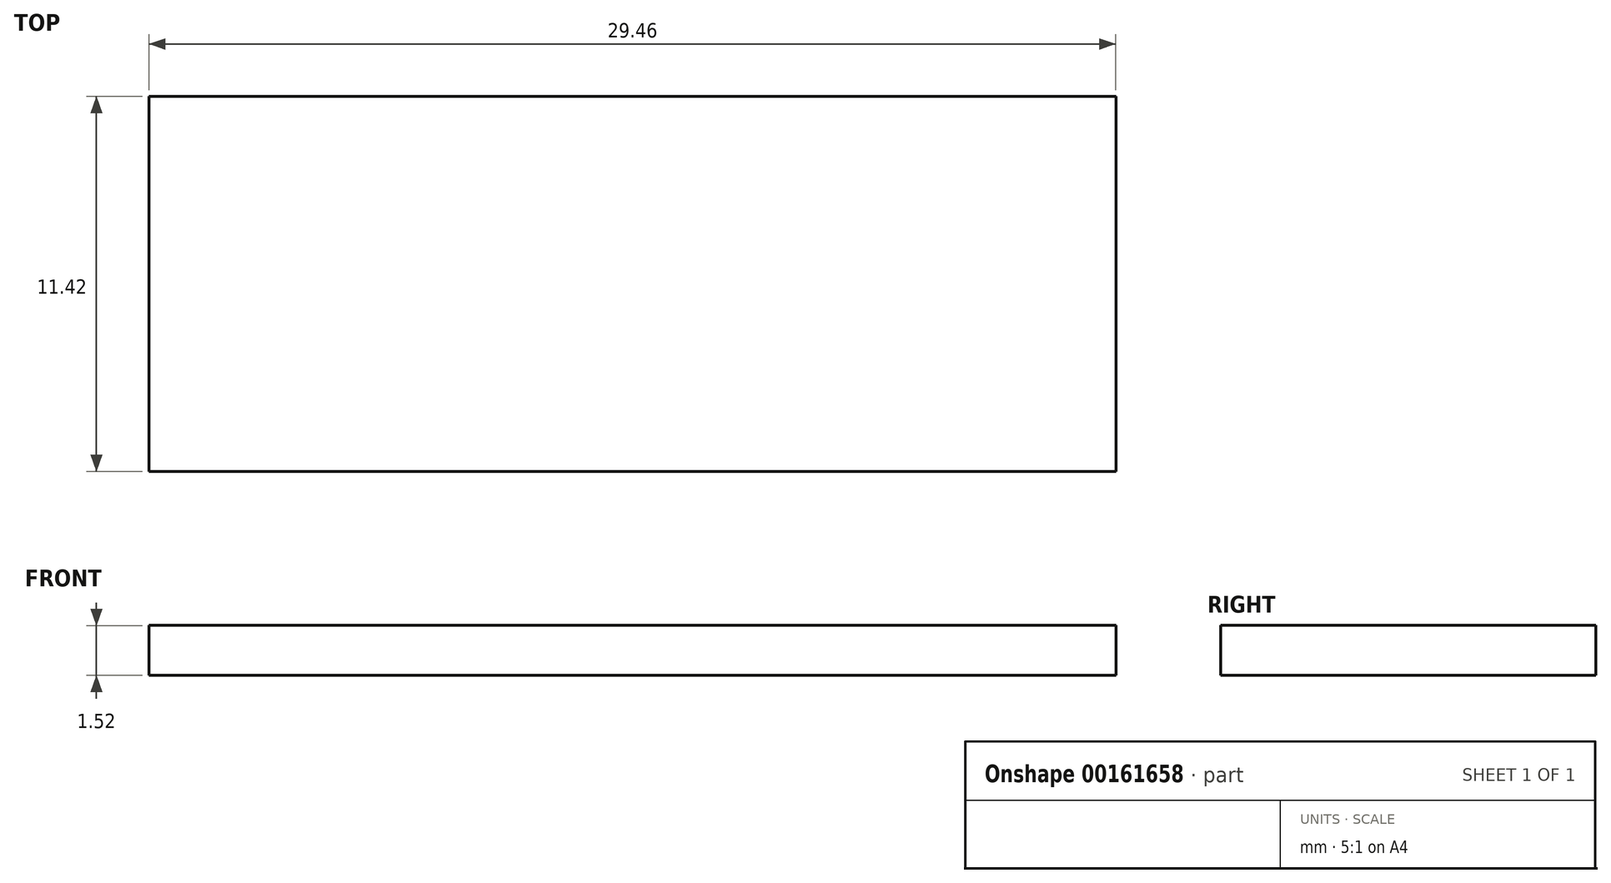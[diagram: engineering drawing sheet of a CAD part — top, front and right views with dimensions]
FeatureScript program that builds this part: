
annotation { "Feature Type Name" : "Feature", "Feature Type Description" : "" }
export const myFeature = defineFeature(function(context is Context, id is Id, definition is map)
    precondition{}
    {
        {
            var Q0;
            Q0=qCreatedBy(makeId("Top.planeOp"),FACE);
            var sketch = newSketch(context, id + "F0", { "sketchPlane" : qUnion([Q0])});
            skLineSegment(sketch, "E0.bottom", {"start": v(-14.73, 5.72) * mm, "end": v(14.73, 5.72) * mm});
            skLineSegment(sketch, "E0.top", {"start": v(-14.73, -5.72) * mm, "end": v(14.73, -5.72) * mm});
            skLineSegment(sketch, "E0.left", {"start": v(-14.73, 5.72) * mm, "end": v(-14.73, -5.72) * mm});
            skLineSegment(sketch, "E0.right", {"start": v(14.73, 5.72) * mm, "end": v(14.73, -5.72) * mm});
            skPoint(sketch, "E0.middle", {"position": v(0, 0) * mm});
            skSolve(sketch);
        }
        {
            var Q0;
            Q0 = qSketchRegion(id + "F0", true);
            extrude(context, id + "F1", {"entities" : qUnion([Q0]), "depth" : 1.52 * mm});
        }
    });
